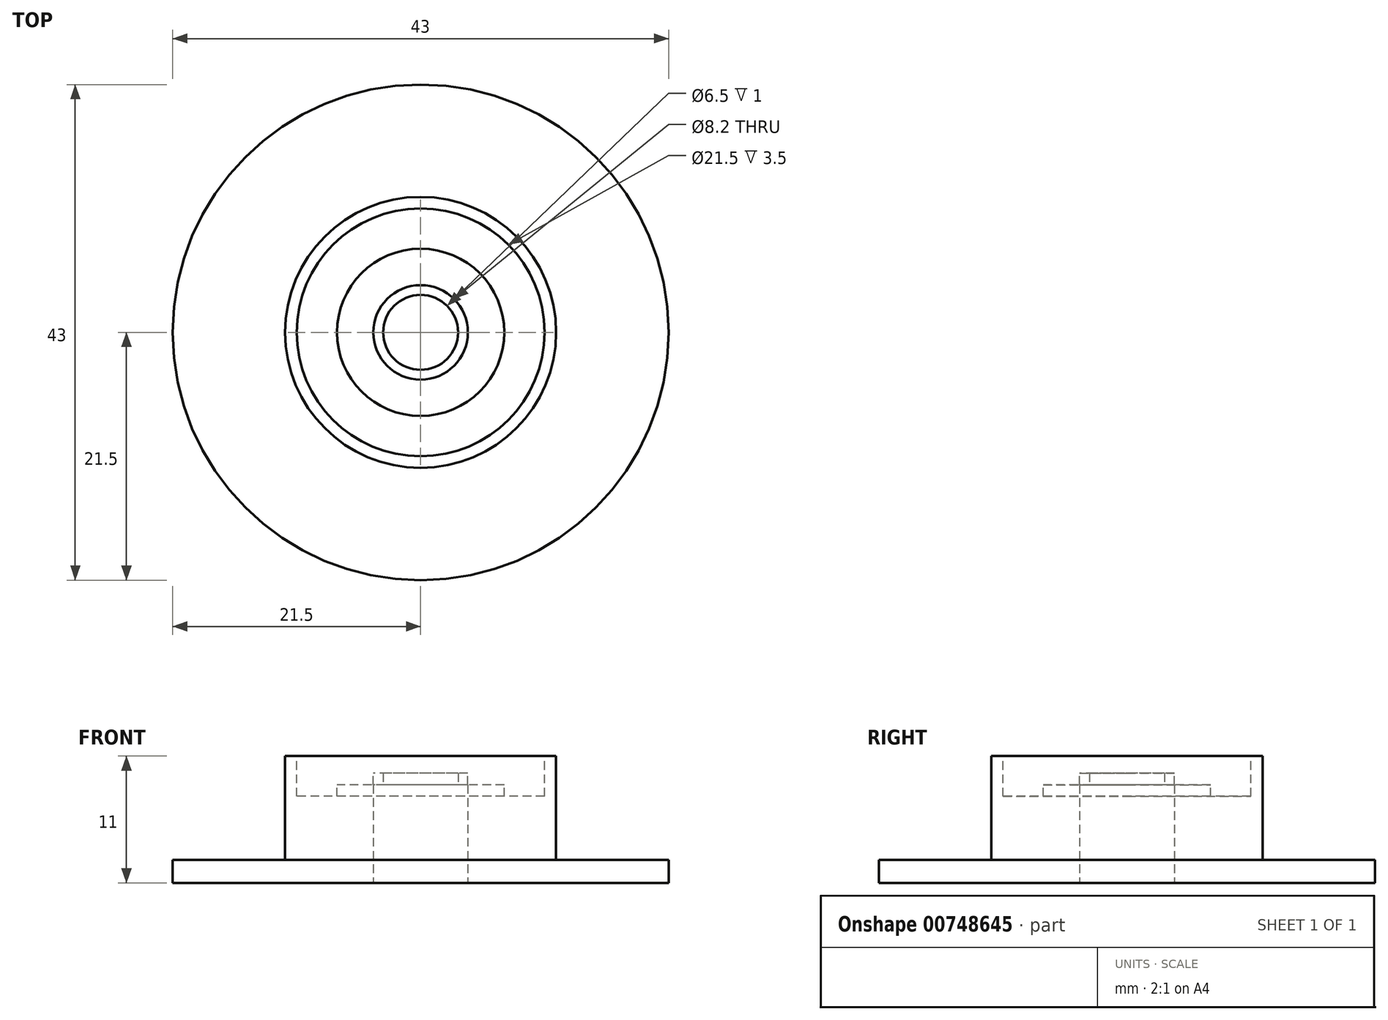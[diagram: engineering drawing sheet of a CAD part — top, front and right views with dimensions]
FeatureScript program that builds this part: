
annotation { "Feature Type Name" : "Feature", "Feature Type Description" : "" }
export const myFeature = defineFeature(function(context is Context, id is Id, definition is map)
    precondition{}
    {
        {
            var Q0;
            Q0=qCreatedBy(makeId("Top.planeOp"),FACE);
            var sketch = newSketch(context, id + "F0", { "sketchPlane" : qUnion([Q0])});
            skCircle(sketch, "E0", {"center": v(0, 0) * mm, "radius": 21.5 * mm});
            skCircle(sketch, "E1", {"center": v(0, 0) * mm, "radius": 4.1 * mm});
            skSolve(sketch);
        }
        {
            var Q0;
            Q0=makeQuery(id+"F0.imprint","IMPRINT",FACE,{"disambiguationData":[TD([[makeQuery(id+"F0.imprint","IMPRINT",EDGE,{"derivedFrom":sQuery(id+"F0.wireOp",EDGE,"E0")}),1.0]])]});
            extrude(context, id + "F1", {"entities" : qUnion([Q0]), "depth" : 2 * mm, "offsetDistance" : 25 * mm});
        }
        {
            var Q0;
            Q0=makeQuery(id+"F1.opExtrude","CAP_FACE",FACE,{"disambiguationData":[OSD([sQuery(id+"F0.wireOp",EDGE,"E0"),sQuery(id+"F0.wireOp",EDGE,"E1")])],"isStart":false});
            var sketch = newSketch(context, id + "F2", { "sketchPlane" : qUnion([Q0])});
            skCircle(sketch, "E2", {"center": v(0, 0) * mm, "radius": 11.75 * mm});
            skSolve(sketch);
        }
        {
            var Q0;
            Q0=makeQuery(id+"F2.imprint","IMPRINT",FACE,{"disambiguationData":[TD([[makeQuery(id+"F2.imprint","IMPRINT",EDGE,{"derivedFrom":sQuery(id+"F2.wireOp",EDGE,"E2")}),1.0]])]});
            extrude(context, id + "F3", {"entities" : qUnion([Q0]), "operationType" : NewBodyOperationType.ADD, "depth" : 9 * mm, "offsetDistance" : 25 * mm});
        }
        {
            var Q0;
            Q0=makeQuery(id+"F3.opExtrude","CAP_FACE",FACE,{"disambiguationData":[OSD([sQuery(id+"F0.wireOp",EDGE,"E1"),sQuery(id+"F2.wireOp",EDGE,"E2")])],"isStart":false});
            var sketch = newSketch(context, id + "F4", { "sketchPlane" : qUnion([Q0])});
            skCircle(sketch, "E3", {"center": v(0, 0) * mm, "radius": 10.75 * mm});
            skCircle(sketch, "E4", {"center": v(0, 0) * mm, "radius": 7.25 * mm});
            skSolve(sketch);
        }
        {
            var Q0;
            Q0=makeQuery(id+"F4.imprint","IMPRINT",FACE,{"disambiguationData":[TD([[makeQuery(id+"F4.imprint","IMPRINT",EDGE,{"derivedFrom":sQuery(id+"F4.wireOp",EDGE,"E3")}),1.0]])]});
            extrude(context, id + "F5", {"entities" : qUnion([Q0]), "operationType" : NewBodyOperationType.REMOVE, "oppositeDirection" : true, "depth" : 3.5 * mm, "offsetDistance" : 25 * mm});
        }
        {
            var Q0;
            {var subQ0=sQuery(id+"F0.wireOp",EDGE,"E1");Q0=makeQuery(id+"F5.boolean.opBoolean","SPLIT",FACE,{"disambiguationData":[TD([makeQuery(id+"F1.opExtrude","SWEPT_FACE",FACE,{"disambiguationData":[OSD([subQ0])]})])],"derivedFrom":makeQuery(id+"F3.opExtrude","CAP_FACE",FACE,{"disambiguationData":[OSD([subQ0,sQuery(id+"F2.wireOp",EDGE,"E2")])],"isStart":false})});}
            extrude(context, id + "F6", {"entities" : qUnion([Q0]), "operationType" : NewBodyOperationType.REMOVE, "oppositeDirection" : true, "depth" : 2.5 * mm, "offsetDistance" : 25 * mm});
        }
        {
            var Q0;
            Q0=makeQuery(id+"F6.boolean.opBoolean","COPY",FACE,{"derivedFrom":makeQuery(id+"F6.opExtrude","CAP_FACE",FACE,{"disambiguationData":[OSD([sQuery(id+"F0.wireOp",EDGE,"E1"),sQuery(id+"F2.wireOp",EDGE,"E2")])],"isStart":false})});
            var sketch = newSketch(context, id + "F7", { "sketchPlane" : qUnion([Q0])});
            skCircle(sketch, "E5", {"center": v(0, 0) * mm, "radius": 3.25 * mm});
            skSolve(sketch);
        }
        {
            var Q0;
            Q0=makeQuery(id+"F7.imprint","IMPRINT",FACE,{"disambiguationData":[TD([[makeQuery(id+"F7.imprint","IMPRINT",EDGE,{"derivedFrom":makeQuery(id+"F6.boolean.opBoolean","COPY",EDGE,{"derivedFrom":makeQuery(id+"F6.opExtrude","CAP_EDGE",EDGE,{"disambiguationData":[OSD([sQuery(id+"F0.wireOp",EDGE,"E1")])],"isStart":false})})}),-1.0]])]});
            var Q1;
            Q1=makeQuery(id+"F7.imprint","IMPRINT",FACE,{"disambiguationData":[TD([[makeQuery(id+"F7.imprint","IMPRINT",EDGE,{"derivedFrom":sQuery(id+"F7.wireOp",EDGE,"E5")}),-1.0]])]});
            extrude(context, id + "F8", {"entities" : qUnion([Q0, Q1]), "operationType" : NewBodyOperationType.ADD, "depth" : 1 * mm, "offsetDistance" : 25 * mm});
        }
    });
